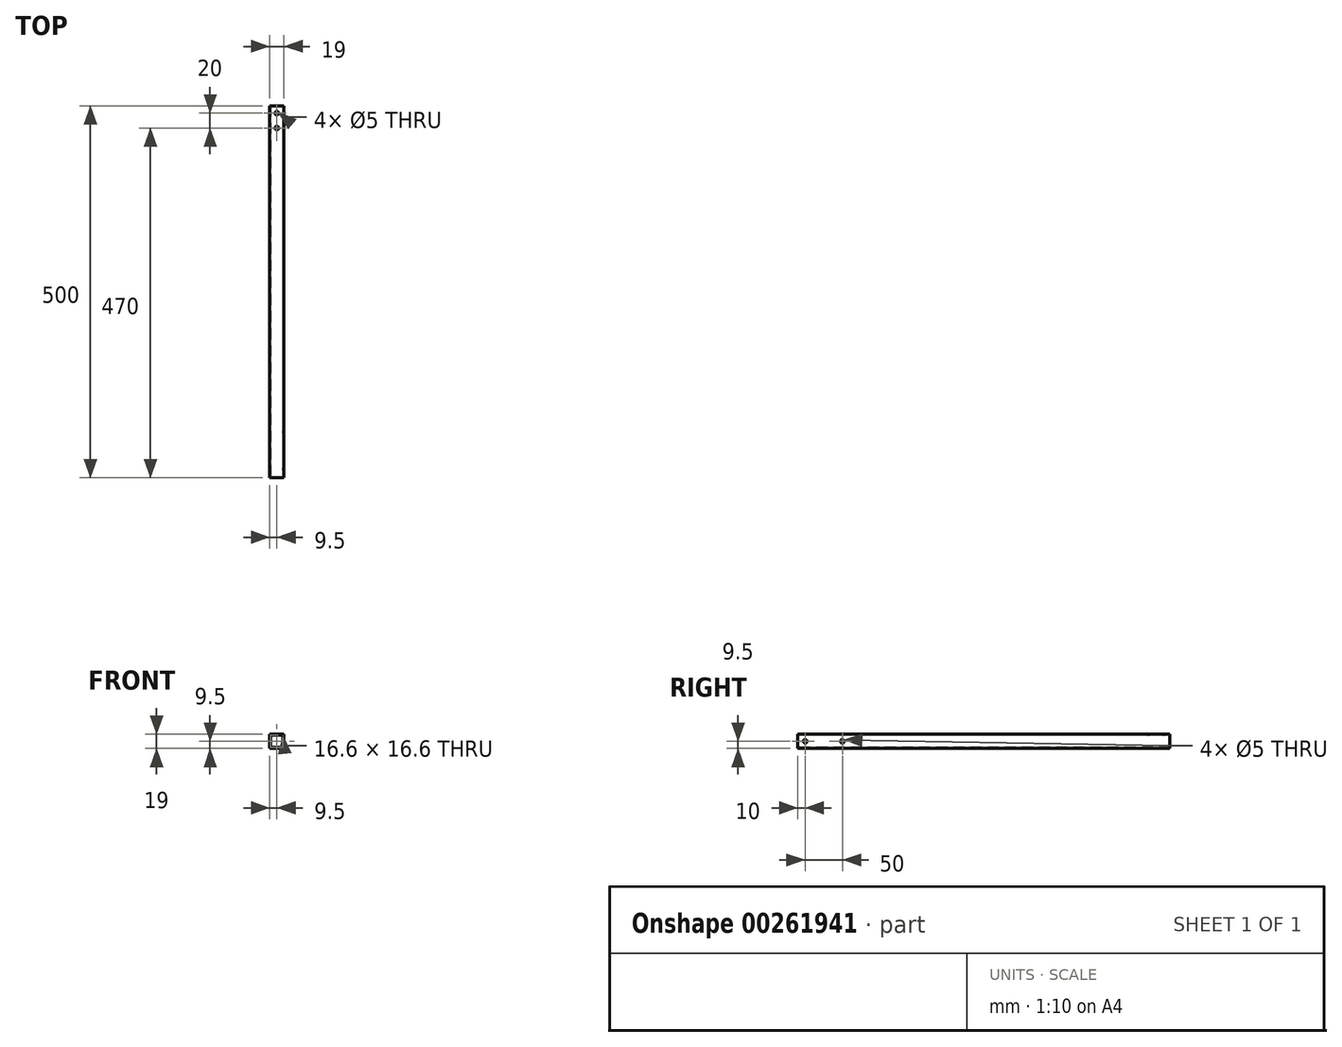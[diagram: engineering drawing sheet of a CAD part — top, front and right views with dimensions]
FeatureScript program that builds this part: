
annotation { "Feature Type Name" : "Feature", "Feature Type Description" : "" }
export const myFeature = defineFeature(function(context is Context, id is Id, definition is map)
    precondition{}
    {
        {
            assignVariable(context, id + "F0", {"name" : "Length", "anyValue" : 500});
        }
        {
            var Q0;
            Q0=qCreatedBy(makeId("Front.planeOp"),FACE);
            var sketch = newSketch(context, id + "F1", { "sketchPlane" : qUnion([Q0])});
            skLineSegment(sketch, "E0.bottom", {"start": v(-9.5, 9.5) * mm, "end": v(9.5, 9.5) * mm});
            skLineSegment(sketch, "E0.top", {"start": v(-9.5, -9.5) * mm, "end": v(9.5, -9.5) * mm});
            skLineSegment(sketch, "E0.left", {"start": v(-9.5, 9.5) * mm, "end": v(-9.5, -9.5) * mm});
            skLineSegment(sketch, "E0.right", {"start": v(9.5, 9.5) * mm, "end": v(9.5, -9.5) * mm});
            skLineSegment(sketch, "E1.bottom", {"start": v(-8.3, 8.3) * mm, "end": v(8.3, 8.3) * mm});
            skLineSegment(sketch, "E1.top", {"start": v(-8.3, -8.3) * mm, "end": v(8.3, -8.3) * mm});
            skLineSegment(sketch, "E1.left", {"start": v(-8.3, 8.3) * mm, "end": v(-8.3, -8.3) * mm});
            skLineSegment(sketch, "E1.right", {"start": v(8.3, 8.3) * mm, "end": v(8.3, -8.3) * mm});
            skSolve(sketch);
        }
        {
            var Q0;
            Q0=qSketchRegion(id+"F1",true);
            extrude(context, id + "F2", {"entities" : qUnion([Q0]), "oppositeDirection" : true, "depth" : (getVariable(context, 'Length')) * mm});
        }
        {
            var Q0;
            Q0=makeQuery(id+"F2.opExtrude","SWEPT_FACE",FACE,{"disambiguationData":[OSD([sQuery(id+"F1.wireOp",EDGE,"E0.bottom")])]});
            var sketch = newSketch(context, id + "F3", { "sketchPlane" : qUnion([Q0])});
            skPoint(sketch, "E2", {"position": v(0, 490) * mm});
            skPoint(sketch, "E2.positionSnap0", {"position": v(0, 500) * mm});
            skPoint(sketch, "E3", {"position": v(0, 470) * mm});
            skSolve(sketch);
        }
        {
            var Q0;
            Q0=sQuery(id+"F3.wireOp",VERTEX,"E2");
            var Q1;
            Q1=sQuery(id+"F3.wireOp",VERTEX,"E3");
            var Q2;
            Q2=makeQuery(id+"F2.opExtrude","SWEPT_BODY",BODY,{"disambiguationData":[OSD([sQuery(id+"F1.wireOp",EDGE,"E0.bottom"),sQuery(id+"F1.wireOp",EDGE,"E0.top"),sQuery(id+"F1.wireOp",EDGE,"E0.left"),sQuery(id+"F1.wireOp",EDGE,"E0.right"),sQuery(id+"F1.wireOp",EDGE,"E1.bottom"),sQuery(id+"F1.wireOp",EDGE,"E1.top"),sQuery(id+"F1.wireOp",EDGE,"E1.left"),sQuery(id+"F1.wireOp",EDGE,"E1.right")])]});
            hole(context, id + "F4", {"style" : HoleStyle.SIMPLE, "endStyle" : HoleEndStyle.THROUGH, "holeDiameter" : 5 * mm, "tappedDepth" : 12 * mm, "tapClearance" : 3, "locations" : qUnion([Q0, Q1]), "scope" : qUnion([Q2])});
        }
        {
            var Q0;
            Q0=makeQuery(id+"F2.opExtrude","SWEPT_FACE",FACE,{"disambiguationData":[OSD([sQuery(id+"F1.wireOp",EDGE,"E0.right")])]});
            var sketch = newSketch(context, id + "F5", { "sketchPlane" : qUnion([Q0])});
            skPoint(sketch, "E4", {"position": v(10, 0) * mm});
            skPoint(sketch, "E5", {"position": v(60, 0) * mm});
            skSolve(sketch);
        }
        {
            var Q0;
            Q0=sQuery(id+"F5.wireOp",VERTEX,"E4");
            var Q1;
            Q1=sQuery(id+"F5.wireOp",VERTEX,"E5");
            var Q2;
            Q2=makeQuery(id+"F2.opExtrude","SWEPT_BODY",BODY,{"disambiguationData":[OSD([sQuery(id+"F1.wireOp",EDGE,"E0.bottom"),sQuery(id+"F1.wireOp",EDGE,"E0.top"),sQuery(id+"F1.wireOp",EDGE,"E0.left"),sQuery(id+"F1.wireOp",EDGE,"E0.right"),sQuery(id+"F1.wireOp",EDGE,"E1.bottom"),sQuery(id+"F1.wireOp",EDGE,"E1.top"),sQuery(id+"F1.wireOp",EDGE,"E1.left"),sQuery(id+"F1.wireOp",EDGE,"E1.right")])]});
            hole(context, id + "F6", {"style" : HoleStyle.SIMPLE, "endStyle" : HoleEndStyle.THROUGH, "holeDiameter" : 5 * mm, "tappedDepth" : 12 * mm, "tapClearance" : 3, "locations" : qUnion([Q0, Q1]), "scope" : qUnion([Q2])});
        }
    });
